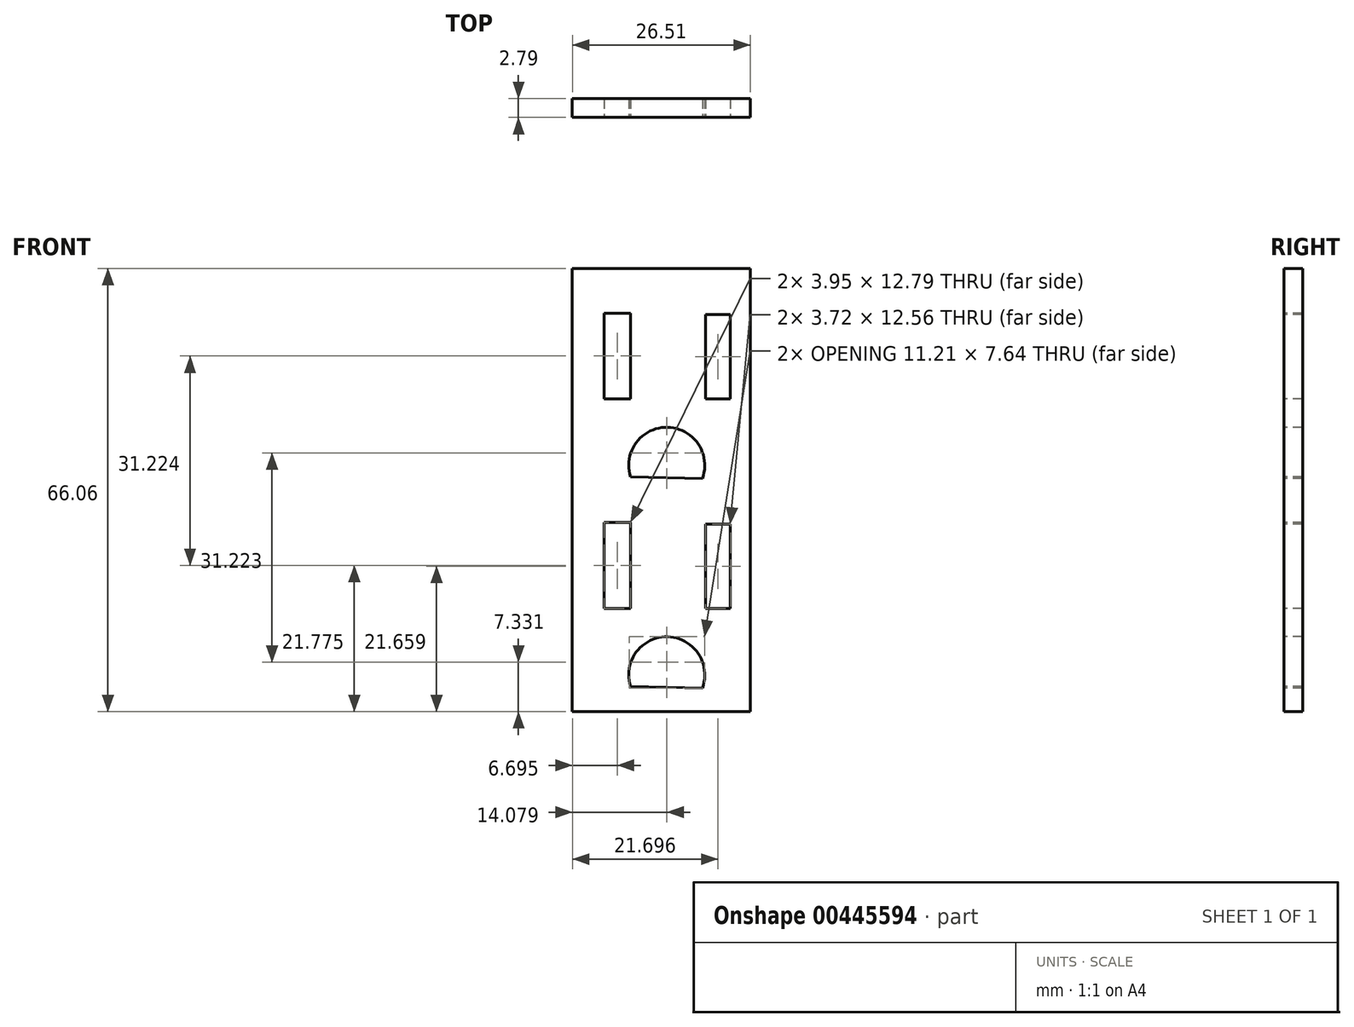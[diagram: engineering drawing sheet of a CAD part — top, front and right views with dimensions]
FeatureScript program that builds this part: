
annotation { "Feature Type Name" : "Feature", "Feature Type Description" : "" }
export const myFeature = defineFeature(function(context is Context, id is Id, definition is map)
    precondition{}
    {
        {
            var Q0;
            Q0=qCreatedBy(makeId("Front.planeOp"),FACE);
            var sketch = newSketch(context, id + "F0", { "sketchPlane" : qUnion([Q0])});
            skLineSegment(sketch, "E0.bottom", {"start": v(35.05, 38.53) * mm, "end": v(8.54, 38.53) * mm});
            skLineSegment(sketch, "E0.top", {"start": v(35.05, -27.53) * mm, "end": v(8.54, -27.53) * mm});
            skLineSegment(sketch, "E0.left", {"start": v(35.05, 38.53) * mm, "end": v(35.05, -27.53) * mm});
            skLineSegment(sketch, "E0.right", {"start": v(8.54, 38.53) * mm, "end": v(8.54, -27.53) * mm});
            skLineSegment(sketch, "E1.bottom", {"start": v(13.26, 31.86) * mm, "end": v(17.21, 31.86) * mm});
            skLineSegment(sketch, "E1.top", {"start": v(13.26, 19.07) * mm, "end": v(17.21, 19.07) * mm});
            skLineSegment(sketch, "E1.left", {"start": v(13.26, 31.86) * mm, "end": v(13.26, 19.07) * mm});
            skLineSegment(sketch, "E1.right", {"start": v(17.21, 31.86) * mm, "end": v(17.21, 19.07) * mm});
            skLineSegment(sketch, "E2.bottom", {"start": v(28.38, 31.63) * mm, "end": v(32.1, 31.63) * mm});
            skLineSegment(sketch, "E2.top", {"start": v(28.38, 19.07) * mm, "end": v(32.1, 19.07) * mm});
            skLineSegment(sketch, "E2.left", {"start": v(28.38, 31.63) * mm, "end": v(28.38, 19.07) * mm});
            skLineSegment(sketch, "E2.right", {"start": v(32.1, 31.63) * mm, "end": v(32.1, 19.07) * mm});
            skArc(sketch, "E3", {"start": v(27.91, 7.2) * mm, "mid": v(22.72, 14.84) * mm, "end": v(17.21, 7.44) * mm});
            skLineSegment(sketch, "E4", {"start": v(17.21, 7.44) * mm, "end": v(27.91, 7.2) * mm});
            skLineSegment(sketch, "E5.bottom", {"start": v(13.26, 0.64) * mm, "end": v(17.21, 0.64) * mm});
            skLineSegment(sketch, "E5.top", {"start": v(13.26, -12.15) * mm, "end": v(17.21, -12.15) * mm});
            skLineSegment(sketch, "E5.left", {"start": v(13.26, 0.64) * mm, "end": v(13.26, -12.15) * mm});
            skLineSegment(sketch, "E5.right", {"start": v(17.21, 0.64) * mm, "end": v(17.21, -12.15) * mm});
            skLineSegment(sketch, "E6.bottom", {"start": v(28.38, 0.4) * mm, "end": v(32.1, 0.4) * mm});
            skLineSegment(sketch, "E6.top", {"start": v(28.38, -12.15) * mm, "end": v(32.1, -12.15) * mm});
            skLineSegment(sketch, "E6.left", {"start": v(28.38, 0.4) * mm, "end": v(28.38, -12.15) * mm});
            skLineSegment(sketch, "E6.right", {"start": v(32.1, 0.4) * mm, "end": v(32.1, -12.15) * mm});
            skArc(sketch, "E7", {"start": v(27.91, -24.02) * mm, "mid": v(22.72, -16.38) * mm, "end": v(17.21, -23.79) * mm});
            skLineSegment(sketch, "E8", {"start": v(17.21, -23.79) * mm, "end": v(27.91, -24.02) * mm});
            skSolve(sketch);
        }
        {
            var Q0;
            Q0=makeQuery(id+"F0.imprint","IMPRINT",FACE,{"disambiguationData":[TD([[makeQuery(id+"F0.imprint","IMPRINT",EDGE,{"derivedFrom":sQuery(id+"F0.wireOp",EDGE,"E0.bottom")}),1.0]])]});
            extrude(context, id + "F1", {"entities" : qUnion([Q0]), "oppositeDirection" : true, "depth" : 2.8 * mm});
        }
    });
